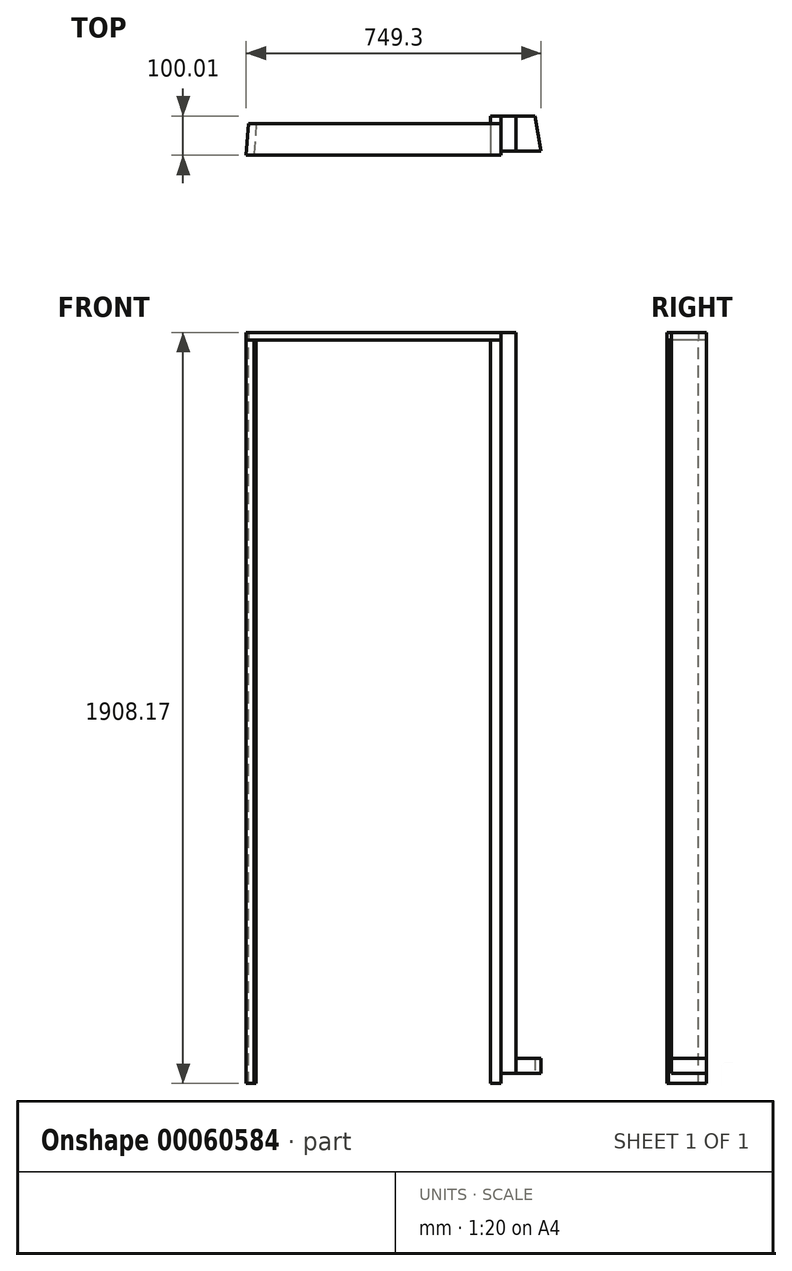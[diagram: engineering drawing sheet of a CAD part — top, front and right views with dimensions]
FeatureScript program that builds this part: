
annotation { "Feature Type Name" : "Feature", "Feature Type Description" : "" }
export const myFeature = defineFeature(function(context is Context, id is Id, definition is map)
    precondition{}
    {
        {
            assignVariable(context, id + "F0", {"name" : "OneByThickness", "anyValue" : 0.78});
        }
        {
            var Q0;
            Q0=qCreatedBy(makeId("Front.planeOp"),FACE);
            var sketch = newSketch(context, id + "F1", { "sketchPlane" : qUnion([Q0])});
            skLineSegment(sketch, "E0.bottom", {"start": v(0, 0) * mm, "end": v(27.3, 0) * mm});
            skLineSegment(sketch, "E0.top", {"start": v(0, 1888.31) * mm, "end": v(27.3, 1888.31) * mm});
            skLineSegment(sketch, "E0.left", {"start": v(0, 0) * mm, "end": v(0, 1888.31) * mm});
            skLineSegment(sketch, "E0.right", {"start": v(27.3, 0) * mm, "end": v(27.3, 1888.31) * mm});
            skSolve(sketch);
        }
        {
            var Q0;
            Q0 = qSketchRegion(id + "F1", true);
            extrude(context, id + "F2", {"entities" : qUnion([Q0]), "oppositeDirection" : true, "depth" : ((3.5 + 7 / 16) - getVariable(context, 'OneByThickness')) * mm});
        }
        {
            var Q0;
            Q0=makeQuery(id+"F2.opExtrude","SWEPT_FACE",FACE,{"disambiguationData":[OSD([sQuery(id+"F1.wireOp",EDGE,"E0.top")])]});
            var sketch = newSketch(context, id + "F3", { "sketchPlane" : qUnion([Q0])});
            skLineSegment(sketch, "E1.bottom", {"start": v(27.3, 100.01) * mm, "end": v(65.4, 100.01) * mm});
            skLineSegment(sketch, "E1.top", {"start": v(27.3, 11.11) * mm, "end": v(65.4, 11.11) * mm});
            skLineSegment(sketch, "E1.left", {"start": v(27.3, 100.01) * mm, "end": v(27.3, 11.11) * mm});
            skLineSegment(sketch, "E1.right", {"start": v(65.4, 100.01) * mm, "end": v(65.4, 11.11) * mm});
            skSolve(sketch);
        }
        {
            var Q0;
            Q0=qCreatedBy(makeId("Top.planeOp"),FACE);
            cPlane(context, id + "F4", {"entities" : qUnion([Q0]), "cplaneType" : CPlaneType.OFFSET, "offset" : 25.4 * mm, "width" : 152.4 * mm, "height" : 152.4 * mm});
        }
        {
            var Q0;
            Q0=makeQuery(id+"F3.imprint","IMPRINT",FACE,{"disambiguationData":[TD([[makeQuery(id+"F3.imprint","IMPRINT",EDGE,{"derivedFrom":sQuery(id+"F3.wireOp",EDGE,"E1.bottom")}),-1.0]])]});
            var Q1;
            Q1=qCreatedBy(id+"F4.planeOp",FACE);
            extrude(context, id + "F5", {"entities" : qUnion([Q0]), "endBound" : BoundingType.UP_TO_SURFACE, "oppositeDirection" : true, "endBoundEntityFace" : qUnion([Q1]), "depth" : 25.4 * mm, "hasSecondDirection" : true, "secondDirectionOppositeDirection" : false, "secondDirectionDepth" : 19.86 * mm});
        }
        {
            var Q0;
            Q0=makeQuery(id+"F2.opExtrude","SWEPT_FACE",FACE,{"disambiguationData":[OSD([sQuery(id+"F1.wireOp",EDGE,"E0.top")])]});
            var sketch = newSketch(context, id + "F6", { "sketchPlane" : qUnion([Q0])});
            skLineSegment(sketch, "E2.bottom", {"start": v(27.3, 80.15) * mm, "end": v(-615.02, 80.15) * mm});
            skLineSegment(sketch, "E2.top", {"start": v(27.3, 0) * mm, "end": v(-620.4, 0) * mm});
            skLineSegment(sketch, "E2.left", {"start": v(27.3, 80.15) * mm, "end": v(27.3, 0) * mm});
            skLineSegment(sketch, "E2.right", {"start": v(-615.02, 80.15) * mm, "end": v(-620.4, 0) * mm});
            skLineSegment(sketch, "E3", {"start": v(-595.11, 80.15) * mm, "end": v(-600.49, 0) * mm});
            skCircle(sketch, "E4", {"center": v(0, 0) * mm, "radius": 597.31 * mm, "construction": true});
            skSolve(sketch);
        }
        {
            var Q0;
            {var subQ2=sQuery(id+"F6.wireOp",EDGE,"hpSSNxMe-q0PY-orQ2-974C-TBJtALFXCPgH");Q0=makeQuery(id+"F6.imprint","IMPRINT",FACE,{"disambiguationData":[TD([[makeQuery(id+"F6.imprint","IMPRINT",EDGE,{"derivedFrom":subQ2}),1.0]])]});}
            var Q1;
            {var subQ2=sQuery(id+"F6.wireOp",EDGE,"E2.left");Q1=makeQuery(id+"F6.imprint","IMPRINT",FACE,{"disambiguationData":[TD([[makeQuery(id+"F6.imprint","IMPRINT",EDGE,{"derivedFrom":subQ2}),-1.0]])]});}
            var Q2;
            {var subQ0=sQuery(id+"F6.wireOp",EDGE,"E2.right");Q2=makeQuery(id+"F6.imprint","IMPRINT",FACE,{"disambiguationData":[TD([[makeQuery(id+"F6.imprint","IMPRINT",EDGE,{"derivedFrom":subQ0}),1.0]])]});}
            var Q3;
            {var subQ2=sQuery(id+"F6.wireOp",EDGE,"E3");Q3=makeQuery(id+"F6.imprint","IMPRINT",FACE,{"disambiguationData":[TD([[makeQuery(id+"F6.imprint","IMPRINT",EDGE,{"derivedFrom":subQ2}),1.0]])]});}
            var Q4;
            Q4=makeQuery(id+"F5.opExtrude","CAP_FACE",FACE,{"disambiguationData":[OSD([sQuery(id+"F3.wireOp",EDGE,"E1.bottom"),sQuery(id+"F3.wireOp",EDGE,"E1.top"),sQuery(id+"F3.wireOp",EDGE,"E1.left"),sQuery(id+"F3.wireOp",EDGE,"E1.right")])],"isStart":true});
            extrude(context, id + "F7", {"entities" : qUnion([Q0, Q1, Q2, Q3]), "endBound" : BoundingType.UP_TO_SURFACE, "endBoundEntityFace" : qUnion([Q4]), "depth" : 25.4 * mm});
        }
        {
            var Q0;
            {var subQ0=sQuery(id+"F6.wireOp",EDGE,"E2.right");Q0=makeQuery(id+"F6.imprint","IMPRINT",FACE,{"disambiguationData":[TD([[makeQuery(id+"F6.imprint","IMPRINT",EDGE,{"derivedFrom":subQ0}),1.0]])]});}
            var Q1;
            Q1=makeQuery(id+"F2.opExtrude","SWEPT_FACE",FACE,{"disambiguationData":[OSD([sQuery(id+"F1.wireOp",EDGE,"E0.bottom")])]});
            var Q2;
            Q2=makeQuery(id+"F7.opExtrude","CAP_FACE",FACE,{"disambiguationData":[OSD([sQuery(id+"F6.wireOp",EDGE,"E2.bottom"),sQuery(id+"F6.wireOp",EDGE,"E2.top"),sQuery(id+"F6.wireOp",EDGE,"E2.left"),sQuery(id+"F6.wireOp",EDGE,"hpSSNxMe-q0PY-orQ2-974C-TBJtALFXCPgH")])],"isStart":false});
            extrude(context, id + "F8", {"entities" : qUnion([Q0]), "endBound" : BoundingType.UP_TO_SURFACE, "oppositeDirection" : true, "endBoundEntityFace" : qUnion([Q1]), "depth" : 1609.03 * mm});
        }
        {
            var Q0;
            Q0=makeQuery(id+"F5.opExtrude","CAP_FACE",FACE,{"disambiguationData":[OSD([sQuery(id+"F3.wireOp",EDGE,"E1.bottom"),sQuery(id+"F3.wireOp",EDGE,"E1.top"),sQuery(id+"F3.wireOp",EDGE,"E1.left"),sQuery(id+"F3.wireOp",EDGE,"E1.right")])],"isStart":false});
            var sketch = newSketch(context, id + "F9", { "sketchPlane" : qUnion([Q0])});
            skLineSegment(sketch, "E5.0", {"start": v(65.4, -11.11) * mm, "end": v(65.4, -100.01) * mm});
            skLineSegment(sketch, "E6", {"start": v(65.4, -11.11) * mm, "end": v(128.9, -11.11) * mm});
            skLineSegment(sketch, "E7", {"start": v(128.9, -11.11) * mm, "end": v(113.23, -100.01) * mm});
            skLineSegment(sketch, "E8", {"start": v(113.23, -100.01) * mm, "end": v(65.4, -100.01) * mm});
            skSolve(sketch);
        }
        {
            var Q0;
            Q0=makeQuery(id+"F9.imprint","IMPRINT",FACE,{"disambiguationData":[TD([[makeQuery(id+"F9.imprint","IMPRINT",EDGE,{"derivedFrom":sQuery(id+"F9.wireOp",EDGE,"E5.0")}),1.0]])]});
            extrude(context, id + "F10", {"entities" : qUnion([Q0]), "oppositeDirection" : true, "depth" : 38.1 * mm});
        }
        {
            var Q0;
            Q0=makeQuery(id+"F2.opExtrude","SWEPT_FACE",FACE,{"disambiguationData":[OSD([sQuery(id+"F1.wireOp",EDGE,"E0.left")])]});
            var sketch = newSketch(context, id + "F11", { "sketchPlane" : qUnion([Q0])});
            skLineSegment(sketch, "E9", {"start": v(-33.66, 1593.04) * mm, "end": v(-33.66, 1681.94) * mm});
            skArc(sketch, "E10", {"start": v(-5.08, 1681.94) * mm, "mid": v(-19.37, 1696.22) * mm, "end": v(-33.66, 1681.94) * mm});
            skLineSegment(sketch, "E11", {"start": v(-5.08, 1681.94) * mm, "end": v(-5.08, 1593.04) * mm});
            skArc(sketch, "E12", {"start": v(-33.66, 1593.04) * mm, "mid": v(-19.37, 1578.75) * mm, "end": v(-5.08, 1593.04) * mm});
            skSolve(sketch);
        }
        {
            var Q0;
            Q0=makeQuery(id+"F11.imprint","IMPRINT",FACE,{"disambiguationData":[TD([[makeQuery(id+"F11.imprint","IMPRINT",EDGE,{"derivedFrom":sQuery(id+"F11.wireOp",EDGE,"E9")}),-1.0]])]});
            extrude(context, id + "F12", {"entities" : qUnion([Q0]), "operationType" : NewBodyOperationType.REMOVE, "oppositeDirection" : true, "depth" : 11.1 * mm});
        }
        {
            var Q0;
            Q0=makeQuery(id+"F2.opExtrude","CAP_FACE",FACE,{"disambiguationData":[OSD([sQuery(id+"F1.wireOp",EDGE,"E0.bottom"),sQuery(id+"F1.wireOp",EDGE,"E0.top"),sQuery(id+"F1.wireOp",EDGE,"E0.left"),sQuery(id+"F1.wireOp",EDGE,"E0.right")])],"isStart":false});
            var sketch = newSketch(context, id + "F13", { "sketchPlane" : qUnion([Q0])});
            skLineSegment(sketch, "E13.2", {"start": v(-27.3, 1908.18) * mm, "end": v(615.02, 1908.18) * mm});
            skLineSegment(sketch, "E14.0", {"start": v(-27.3, 1908.18) * mm, "end": v(-27.3, 1888.31) * mm});
            skLineSegment(sketch, "E15.0", {"start": v(-27.3, 0) * mm, "end": v(-27.3, 1888.31) * mm});
            skLineSegment(sketch, "E16", {"start": v(628.83, 0) * mm, "end": v(590.73, 0) * mm});
            skLineSegment(sketch, "E17", {"start": v(590.73, 0) * mm, "end": v(590.73, 1851.02) * mm});
            skLineSegment(sketch, "E18", {"start": v(590.73, 1851.02) * mm, "end": v(10.8, 1851.02) * mm});
            skLineSegment(sketch, "E19", {"start": v(10.8, 1851.02) * mm, "end": v(10.8, 0) * mm});
            skLineSegment(sketch, "E20", {"start": v(10.8, 0) * mm, "end": v(-27.3, 0) * mm});
            skLineSegment(sketch, "E21", {"start": v(0, 132.94) * mm, "end": v(10.8, 132.94) * mm, "construction": true});
            skLineSegment(sketch, "E22", {"start": v(590.73, 141.48) * mm, "end": v(601.52, 141.48) * mm, "construction": true});
            skLineSegment(sketch, "E23", {"start": v(628.83, 0) * mm, "end": v(628.83, 1889.12) * mm});
            skLineSegment(sketch, "E24", {"start": v(621.43, 1889.12) * mm, "end": v(628.83, 1889.12) * mm});
            skSolve(sketch);
        }
        {
            var Q0;
            Q0=makeQuery(id+"F13.imprint","IMPRINT",FACE,{"disambiguationData":[TD([[makeQuery(id+"F13.imprint","IMPRINT",EDGE,{"derivedFrom":sQuery(id+"F13.wireOp",EDGE,"E13.0")}),1.0]])]});
            var Q1;
            {var subQ0=sQuery(id+"F13.wireOp",EDGE,"E15.0");Q1=makeQuery(id+"F13.imprint","IMPRINT",FACE,{"disambiguationData":[TD([[makeQuery(id+"F13.imprint","IMPRINT",EDGE,{"derivedFrom":subQ0}),-1.0]])]});}
            var Q2;
            Q2=makeQuery(id+"F13.imprint","IMPRINT",FACE,{"disambiguationData":[TD([[makeQuery(id+"F13.imprint","IMPRINT",EDGE,{"derivedFrom":sQuery(id+"F13.wireOp",EDGE,"E13.2")}),-1.0]])]});
            var Q3;
            Q3=makeQuery(id+"F5.opExtrude","SWEPT_FACE",FACE,{"disambiguationData":[OSD([sQuery(id+"F3.wireOp",EDGE,"E1.bottom")])]});
            extrude(context, id + "F14", {"entities" : qUnion([Q0, Q1, Q2]), "endBound" : BoundingType.UP_TO_SURFACE, "endBoundEntityFace" : qUnion([Q3]), "depth" : 25.4 * mm});
        }
    });
